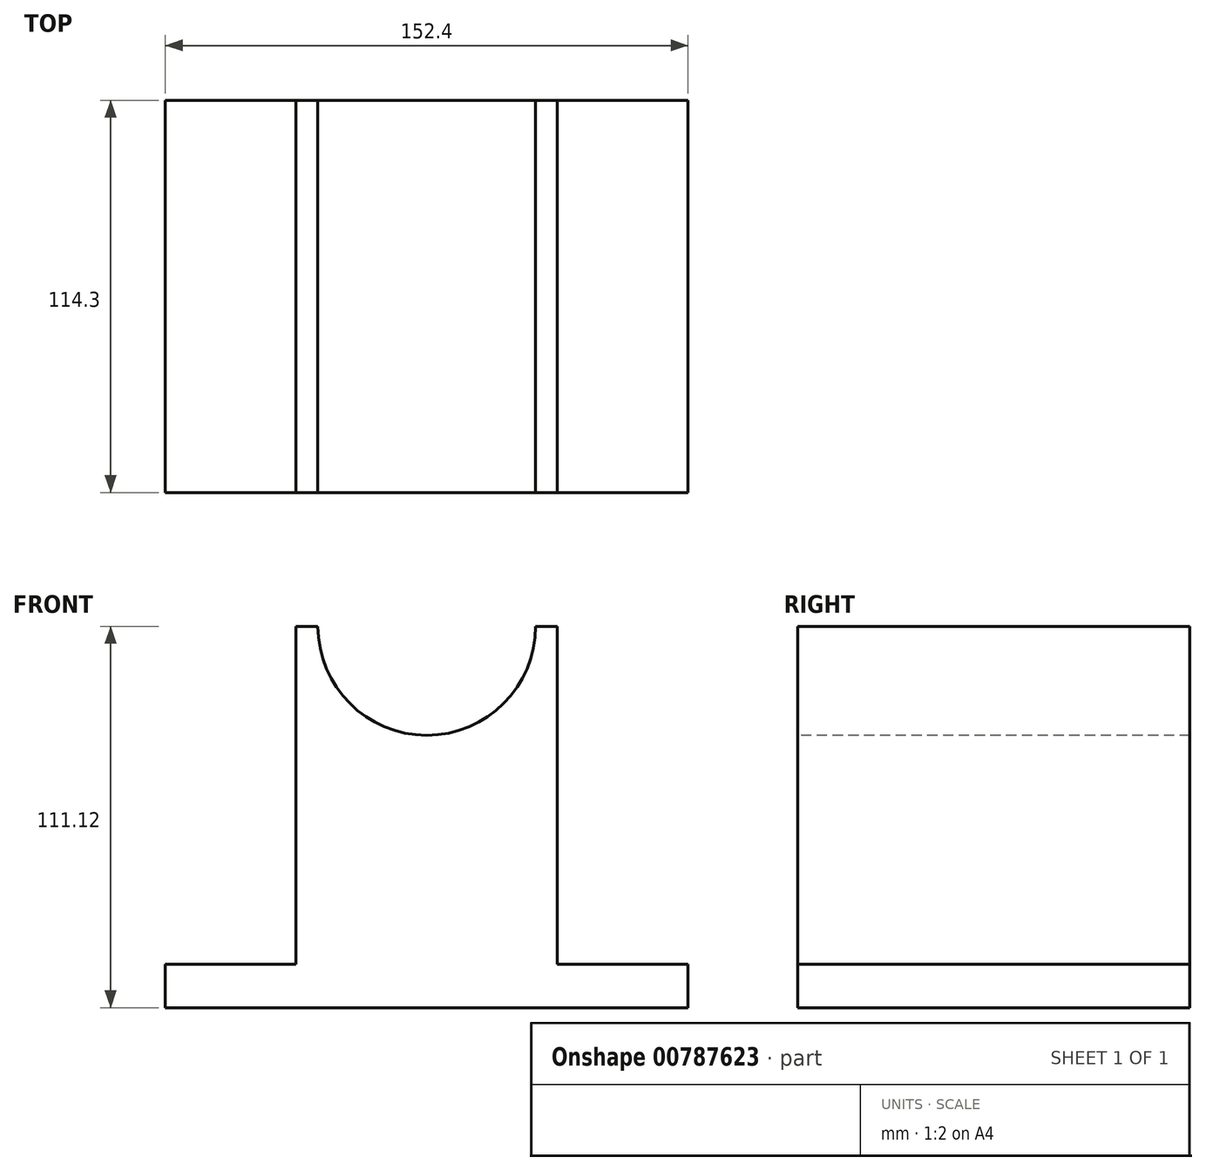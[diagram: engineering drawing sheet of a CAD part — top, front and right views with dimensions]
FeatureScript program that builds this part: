
annotation { "Feature Type Name" : "Feature", "Feature Type Description" : "" }
export const myFeature = defineFeature(function(context is Context, id is Id, definition is map)
    precondition{}
    {
        {
            var Q0;
            Q0=qCreatedBy(makeId("Front.planeOp"),FACE);
            var sketch = newSketch(context, id + "F0", { "sketchPlane" : qUnion([Q0])});
            skLineSegment(sketch, "E0", {"start": v(0, 0) * mm, "end": v(152.4, 0) * mm});
            skLineSegment(sketch, "E1", {"start": v(152.4, 0) * mm, "end": v(152.4, 12.7) * mm});
            skLineSegment(sketch, "E2", {"start": v(152.4, 12.7) * mm, "end": v(114.3, 12.7) * mm});
            skLineSegment(sketch, "E3", {"start": v(114.3, 12.7) * mm, "end": v(114.3, 111.12) * mm});
            skLineSegment(sketch, "E4", {"start": v(114.3, 111.12) * mm, "end": v(38.1, 111.12) * mm});
            skLineSegment(sketch, "E5", {"start": v(38.1, 111.12) * mm, "end": v(38.1, 12.7) * mm});
            skLineSegment(sketch, "E6", {"start": v(38.1, 12.7) * mm, "end": v(0, 12.7) * mm});
            skLineSegment(sketch, "E7", {"start": v(0, 12.7) * mm, "end": v(0, 0) * mm});
            skSolve(sketch);
        }
        {
            var Q0;
            Q0=makeQuery(id+"F0.imprint","IMPRINT",FACE,{"disambiguationData":[TD([[makeQuery(id+"F0.imprint","IMPRINT",EDGE,{"derivedFrom":sQuery(id+"F0.wireOp",EDGE,"E0")}),1.0]])]});
            extrude(context, id + "F1", {"entities" : qUnion([Q0]), "depth" : 114.3 * mm, "offsetDistance" : 25.4 * mm});
        }
        {
            var Q0;
            Q0=makeQuery(id+"F1.opExtrude","CAP_FACE",FACE,{"disambiguationData":[OSD([sQuery(id+"F0.wireOp",EDGE,"E0"),sQuery(id+"F0.wireOp",EDGE,"E1"),sQuery(id+"F0.wireOp",EDGE,"E2"),sQuery(id+"F0.wireOp",EDGE,"E3"),sQuery(id+"F0.wireOp",EDGE,"E4"),sQuery(id+"F0.wireOp",EDGE,"E5"),sQuery(id+"F0.wireOp",EDGE,"E6"),sQuery(id+"F0.wireOp",EDGE,"E7")])],"isStart":false});
            var sketch = newSketch(context, id + "F2", { "sketchPlane" : qUnion([Q0])});
            skLineSegment(sketch, "E8", {"start": v(76.2, 111.12) * mm, "end": v(107.95, 111.12) * mm, "construction": true});
            skLineSegment(sketch, "E9", {"start": v(76.2, 111.12) * mm, "end": v(44.45, 111.12) * mm, "construction": true});
            skArc(sketch, "E10", {"start": v(44.45, 111.12) * mm, "mid": v(76.2, 79.38) * mm, "end": v(107.95, 111.12) * mm});
            skSolve(sketch);
        }
        {
            var Q0;
            {var subQ0=sQuery(id+"F2.wireOp",EDGE,"E10");Q0=makeQuery(id+"F2.imprint","IMPRINT",FACE,{"disambiguationData":[TD([[makeQuery(id+"F2.imprint","IMPRINT",EDGE,{"derivedFrom":subQ0}),1.0]])]});}
            extrude(context, id + "F3", {"entities" : qUnion([Q0]), "operationType" : NewBodyOperationType.REMOVE, "endBound" : BoundingType.THROUGH_ALL, "oppositeDirection" : true, "depth" : 25.4 * mm, "offsetDistance" : 25.4 * mm});
        }
    });
